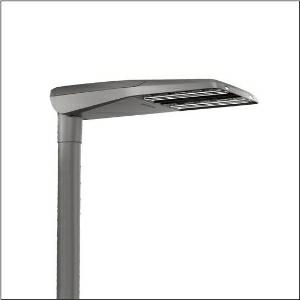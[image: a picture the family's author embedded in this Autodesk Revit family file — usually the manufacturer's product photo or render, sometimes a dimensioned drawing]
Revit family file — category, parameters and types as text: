
# Revit family: streetlight_sl_11_iq_midi___st1_2p1_0_5xc3g41f08me_0c33
name_source: partatom
category: Lighting Fixtures
units: mm (PartAtom-declared; Revit-internal decimal feet)

## family parameters
Cut with Voids When Loaded = No
Host = Face
Light Source = No
Part Type = Normal
Room Calculation Point = No
Round Connector Dimension = Use Diameter
Shared = No

## types (1)
- --- (1 x LED, 18520 lm, 124.7 W, 4000K)
    Apparent Load = 125 VA
    CIE Flux Codes = 31 68 95 100 100
    Color Rendering = 70
    Color Temperature = 4000K
    Default Elevation = 1800 mm
    Description = Streetlight SL 11 iQ midi, mast luminaire, primary light control with 3 zone facetted reflector, of plastic, silver coated, highly specular, primary optical cover: cover, of PMMA, transparent, light distribution: ST1.2P1.0, light emission: direct distribution, primary light characteristic: asymmetric, installation type: post-top, side-entry, LED, High Power LED, rated luminous flux: 18.520lm, luminous efficacy: 149lm/W, light colour: 740, colour temperature: 4000K, control: Street-Remote, optimised constant luminous flux control (CLO 2.0), Auto-Match, Desk-Remote (wireless, voltage-free reading and setting of iQ features in the workshop via application-optimized NFC function/RFID function), Light-Fading, Smart-Wire, Night-Set, Lumen-Switch, Temp-Guard, with cable H07RN-F 5x 1.5mm², mains connection: 220..240V, AC, 50/60Hz, connection cable pre-assembled, cable length: 12,5m, start of lifetime: 125W, end of lifetime: 132W, reduction: 57W, luminaire housing, of diecast aluminium, powder-coated, Siteco® metallic grey (DB 702S), length: 780mm, width: 376mm, height: 118mm, spigot size: 60/76mm (post-top) and 42/60/76mm (side-entry), mast flange for spigot size: 42mm: 5XC10008XM4, 60mm: 5XC10008XM2, 76/60mm: 5XC10108XM1, equipment: Power, protection rating (complete): IP66, insulation class (complete): insulation class II (safety insulation), certification: CE, ENEC, VDE, impact resistance: IK09, permissible operating ambient temperature for outdoor applications: -25..+50°C, standard-compliant lighting for roads and squares, packaging unit: 1 piece

Light Distribution: ST1.2P1.0
    Height = 118 mm
    Lamp = 1 x LED
    Lamp Light Flux = 18520 lm
    Lamp Power = 124.7 W
    Lamp count = 1
    Length = 780 mm
    Luminous efficacy = 149 lm/W
    Manufacturer = Siteco
    ModVariant = No
    Model = 5XC3G41F08ME
    Number of Poles = 1
    OnlyDefault = Yes
    Power Factor = 1
    Product Name = Streetlight SL 11 iQ midi | ST1.2P1.0
    Product group = mast luminaire | pylon top
    ProductGroupID = 6100
    Protection Class = Protection class II
    Protection Degree = IP 66
    RLX_Detail_Level = 1
    RlxData = <blob elided: 70297 chars, md5=2efe485f>
    Socket = socket
    Standby Power = 0 W
    System Light Flux = 18520 lm
    System Power = 125 W
    Type Comments = factory setting: luminous flux: 100 % | dim-lin: 254 | 557 mA
    Type Image = l_1005960.jpg
    URL = http://relux.com
    VarID = @adj_116209
    Voltage = 0 V
    Weight = 0.00 kg
    Width = 376 mm

## geometry (parser evidence)
native form markers: Blend x4, Sweep x10
no freeform markers — native parametric forms only
